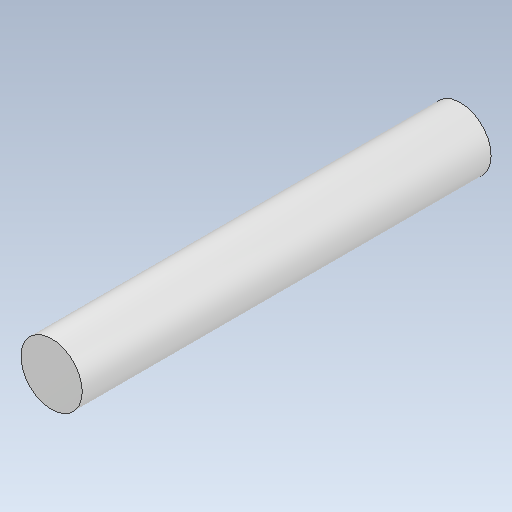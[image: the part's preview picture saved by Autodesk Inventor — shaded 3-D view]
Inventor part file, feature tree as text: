
AUTODESK INVENTOR PART (.ipt)
format: ipt  version: 2020 (Build 240168000, 168)  size: 98,304 bytes
history: native  units: mm
features: other x1, extrude x1, sketch x1
ambient origin geometry x8: Origin, YZ Plane, XZ Plane, XY Plane, X Axis, Y Axis, Z Axis, Center Point
bodies: Body1 (feature_tree)
feature tree (3):
  other  "ソリッド1"
  extrude  "押し出し1"  Depth=3.0mm
  sketch  "スケッチ1"
